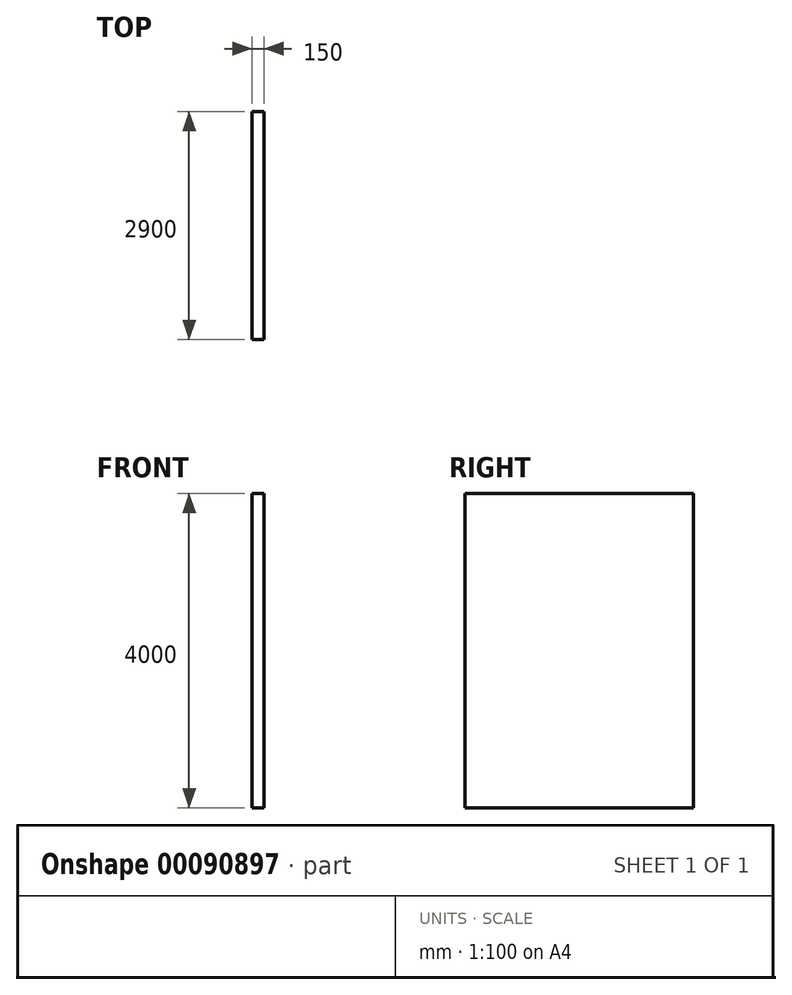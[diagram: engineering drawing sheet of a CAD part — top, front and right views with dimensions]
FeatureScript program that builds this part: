
annotation { "Feature Type Name" : "Feature", "Feature Type Description" : "" }
export const myFeature = defineFeature(function(context is Context, id is Id, definition is map)
    precondition{}
    {
        {
            var Q0;
            Q0=qCreatedBy(makeId("Right.planeOp"),FACE);
            var sketch = newSketch(context, id + "F0", { "sketchPlane" : qUnion([Q0])});
            skLineSegment(sketch, "E0.bottom", {"start": v(-1451.39, 2236.62) * mm, "end": v(1448.61, 2236.62) * mm});
            skLineSegment(sketch, "E0.top", {"start": v(-1451.39, -1763.38) * mm, "end": v(1448.61, -1763.38) * mm});
            skLineSegment(sketch, "E0.left", {"start": v(-1451.39, 2236.62) * mm, "end": v(-1451.39, -1763.38) * mm});
            skLineSegment(sketch, "E0.right", {"start": v(1448.61, 2236.62) * mm, "end": v(1448.61, -1763.38) * mm});
            skSolve(sketch);
        }
        {
            var Q0;
            Q0 = qSketchRegion(id + "F0", true);
            extrude(context, id + "F1", {"entities" : qUnion([Q0]), "depth" : 150 * mm});
        }
    });
